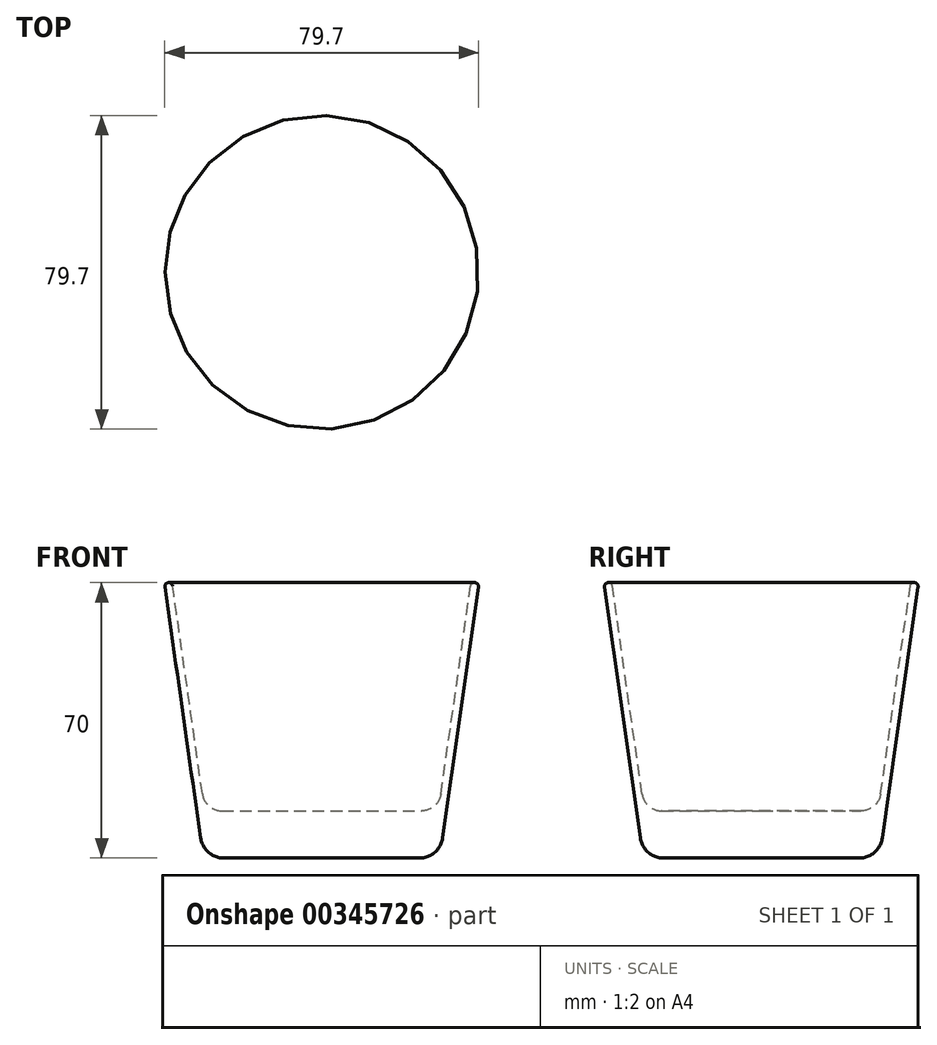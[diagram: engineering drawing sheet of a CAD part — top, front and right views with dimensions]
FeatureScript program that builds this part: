
annotation { "Feature Type Name" : "Feature", "Feature Type Description" : "" }
export const myFeature = defineFeature(function(context is Context, id is Id, definition is map)
    precondition{}
    {
        {
            var Q0;
            Q0=qCreatedBy(makeId("Front.planeOp"),FACE);
            var sketch = newSketch(context, id + "F0", { "sketchPlane" : qUnion([Q0])});
            skLineSegment(sketch, "E0", {"start": v(0, 0) * mm, "end": v(24.8, 0) * mm});
            skLineSegment(sketch, "E1", {"start": v(30.74, 5.15) * mm, "end": v(39.84, 68.86) * mm});
            skPoint(sketch, "E2.visualSharp", {"position": v(30, 0) * mm});
            skArc(sketch, "E2.filletArc", {"start": v(24.8, 0) * mm, "mid": v(28.73, 1.47) * mm, "end": v(30.74, 5.15) * mm});
            skLineSegment(sketch, "E3.0", {"start": v(30.3, 16.3) * mm, "end": v(37.86, 69.14) * mm});
            skLineSegment(sketch, "E4.0", {"start": v(0, 12) * mm, "end": v(25.36, 12) * mm});
            skArc(sketch, "E5.filletArc", {"start": v(25.36, 12) * mm, "mid": v(28.63, 13.22) * mm, "end": v(30.3, 16.3) * mm});
            skArc(sketch, "E6", {"start": v(39.84, 68.86) * mm, "mid": v(38.99, 69.99) * mm, "end": v(37.86, 69.14) * mm});
            skPoint(sketch, "E6.first.point", {"position": v(37.86, 69.14) * mm});
            skPoint(sketch, "E6.second.point", {"position": v(38.85, 70) * mm});
            skPoint(sketch, "E6.third.point", {"position": v(39.84, 68.86) * mm});
            skPoint(sketch, "E7.orphan", {"position": v(40, 70) * mm});
            skLineSegment(sketch, "E8", {"start": v(0, 0) * mm, "end": v(0, 12) * mm});
            skSolve(sketch);
        }
        {
            var Q0;
            Q0=makeQuery(id+"F0.imprint","IMPRINT",FACE,{"disambiguationData":[TD([[makeQuery(id+"F0.imprint","IMPRINT",EDGE,{"derivedFrom":sQuery(id+"F0.wireOp",EDGE,"E0")}),1.0]])]});
            var Q1;
            Q1=sQuery(id+"F0.wireOp",EDGE,"E8");
            revolve(context, id + "F1", {"entities" : qUnion([Q0]), "axis" : qUnion([Q1]), "revolveType" : RevolveType.FULL});
        }
    });
